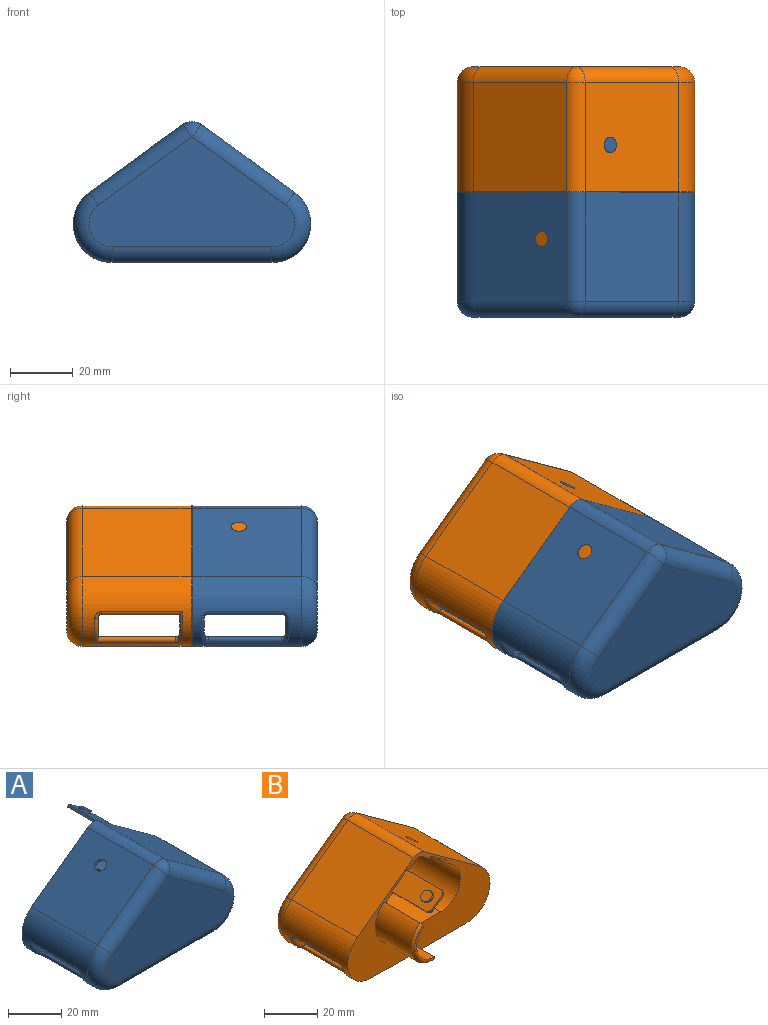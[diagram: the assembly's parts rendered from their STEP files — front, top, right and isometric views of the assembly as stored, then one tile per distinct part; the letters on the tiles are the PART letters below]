
ASSEMBLY  parts=2 mates=1
PART A: 71 faces, bbox 77.8x60x46 mm
  f0: cylinder r=1mm len=23.45mm, axis (0,-1,0), area 62.9mm2, adj f1,f13,f53,f62
  f1: bspline ~2.2x1.73mm, area 3.7mm2, adj f0,f13,f53,f55,f57
  f2: cylinder r=1mm len=23.45mm, axis (0,-1,0), area 62.9mm2, adj f3,f6,f12,f53
  f3: bspline ~2.2x1.73mm, area 3.7mm2, adj f2,f5,f12,f53,f57
  f4: bspline ~3.05x2.82mm, area 4mm2, adj f13,f58,f62,f65
  f5: bspline ~3.05x2.82mm, area 4mm2, adj f3,f12,f57,f61
  f6: bspline ~2.2x1.73mm, area 3.7mm2, adj f2,f12,f53,f65,f68
  f7: plane 75.76x45mm, normal (0,1,0), area 1366.3mm2, adj f8,f9,f10,f12,f13,f14,f15,f16
  f8: plane 51.04x35mm, normal (0,0,-1), area 1786.4mm2, adj f7,f12,f13,f25
  f9: plane 35x29.85mm, normal (0.59,0,0.81), area 1291.2mm2, adj f7,f12,f14,f26
  f10: plane 35x29.85mm, normal (-0.59,0,0.81), area 1271.6mm2, adj f7,f13,f14,f22,f32
  f11: plane 65.76x35mm, normal (0,-1,0), area 1488.7mm2, adj f22,f23,f25,f26,f27
  f12: cylinder r=12.36mm len=35mm, axis (0,-1,0), area 748.5mm2, adj f2,f3,f5,f6,f7,f8,f9,f27
  f13: cylinder r=12.36mm len=35mm, axis (0,-1,0), area 748.5mm2, adj f0,f1,f4,f7,f8,f10,f23,f54
  f14: cylinder r=5mm len=35mm, axis (0,1,0), area 219.9mm2, adj f7,f9,f10,f24
  f15: plane 38x20.51mm, normal (0,0,1), area 779.4mm2, adj f7,f18,f20,f46
  f16: plane 58x13.66mm, normal (-0.59,0,-0.81), area 841.2mm2, adj f7,f18,f21,f35,f36,f38,f48,f49
  f17: plane 38x16.08mm, normal (0.59,0,-0.81), area 552.1mm2, adj f7,f18,f20,f21,f28,f29,f31,f33
  f18: plane 44.23x31mm, normal (0,1,0), area 991.7mm2, adj f15,f16,f17,f19,f20,f21,f46,f48
  f19: cylinder r=10.36mm len=19.66mm, axis (0,-1,0), area 444mm2, adj f18,f46,f47,f48
  f20: cylinder r=10.36mm len=38mm, axis (0,-1,0), area 989.5mm2, adj f7,f15,f17,f18
  f21: cylinder r=3mm len=38mm, axis (0,1,0), area 143.3mm2, adj f7,f16,f17,f18
  f22: cylinder r=5mm len=32.79mm, axis (0.81,0,0.59), area 289.7mm2, adj f10,f11,f23,f24
  f23: torus R=7.36mm, axis (0,-1,0), area 208.1mm2, adj f11,f13,f22,f25
  f24: sphere r=5mm, area 48.5mm2, adj f14,f22,f26
  f25: cylinder r=5mm len=51.04mm, axis (-1,0,0), area 400.9mm2, adj f8,f11,f23,f27
  f26: cylinder r=5mm len=32.79mm, axis (0.81,0,-0.59), area 289.7mm2, adj f9,f11,f24,f27
  f27: torus R=7.36mm, axis (0,-1,0), area 208.1mm2, adj f11,f12,f25,f26
  f28: plane 18.5x0.81mm, normal (0.81,0,0.59), area 18.5mm2, adj f7,f17,f30,f33
  f29: plane 18.5x0.81mm, normal (-0.81,0,-0.59), area 18.5mm2, adj f7,f17,f30,f34
  f30: plane 20.5x8.09mm, normal (0.59,0,-0.81), area 183.6mm2, adj f7,f28,f29,f31,f32,f33,f34
  f31: plane 5.44x4.34mm, normal (0,1,0), area 6mm2, adj f17,f30,f33,f34
  f32: cylinder r=2.5mm len=5mm, axis (-0.59,0,0.81), area 15.7mm2, adj f10,f30
  f33: cylinder r=2mm len=2.21mm, axis (0.59,0,-0.81), area 3.1mm2, adj f17,f28,f30,f31
  f34: cylinder r=2mm len=2.21mm, axis (-0.59,0,0.81), area 3.1mm2, adj f17,f29,f30,f31
  f35: plane 19x0.81mm, normal (-0.81,0,0.59), area 19mm2, adj f7,f16,f37,f49
  f36: plane 20x0.81mm, normal (0.81,0,-0.59), area 20mm2, adj f7,f16,f37,f38
  f37: plane 20x8.09mm, normal (0.59,0,0.81), area 181.7mm2, adj f7,f35,f36,f38,f39,f49
  f38: plane 7.87x6.1mm, normal (0,1,0), area 9mm2, adj f16,f36,f37,f49
  f39: cylinder r=2.4mm len=4.8mm, axis (-0.59,0,-0.81), area 15.1mm2, adj f37,f40
  f40: plane 4.8x3.88mm, normal (0.59,0,0.81), area 18.1mm2, adj f39
  f41: cylinder r=10.36mm len=19mm, axis (0,-1,0), area 494.7mm2, adj f7,f42,f43,f45
  f42: plane 20x0.81mm, normal (-0.81,0,0.59), area 19.5mm2, adj f7,f41,f44,f45
  f43: plane 20x1mm, normal (-1,0,0), area 19.5mm2, adj f7,f41,f44,f45
  f44: cylinder r=9.36mm len=40mm, axis (0,-1,0), area 941mm2, adj f42,f43,f45,f46,f47,f48
  f45: cone r=9.36mm half-angle=45deg, axis (0,-1,0), area 35mm2, adj f41,f42,f43,f44
  f46: cylinder r=5mm len=38mm, axis (0,-1,0), area 89.6mm2, adj f7,f15,f18,f19,f44,f47
  f47: torus R=5.36mm, axis (0,1,0), area 86.7mm2, adj f19,f44,f46,f48
  f48: cylinder r=5mm len=38mm, axis (0,-1,0), area 89.6mm2, adj f7,f16,f18,f19,f44,f47
  f49: cylinder r=1mm len=1.4mm, axis (0.59,0,0.81), area 1.6mm2, adj f16,f35,f37,f38
  f50: plane 72.85x5mm, normal (0,-1,0), area 352.1mm2, adj f58,f65,f66,f70
  f51: plane 73.64x24mm, normal (0,0,-1), area 1767.3mm2, adj f59,f60,f66,f67
  f52: plane 72.85x5mm, normal (0,1,0), area 352.1mm2, adj f54,f57,f60,f61
  f53: plane 61.12x24mm, normal (0,0,1), area 1467mm2, adj f0,f1,f2,f3,f6,f57,f62,f65
  f54: torus R=11.36mm, axis (0,1,0), area 9.8mm2, adj f13,f52,f55,f56
  f55: bspline ~3.14x2.61mm, area 4mm2, adj f1,f13,f54,f57
  f56: bspline ~2.49x2.45mm, area 3.4mm2, adj f13,f54,f59,f60
  f57: cylinder r=1mm len=66.81mm, axis (-1,0,0), area 99.9mm2, adj f1,f3,f5,f52,f53,f55
  f58: torus R=11.36mm, axis (0,1,0), area 9.8mm2, adj f4,f13,f50,f63
  f59: cylinder r=1mm len=24mm, axis (0,-1,0), area 35.2mm2, adj f13,f51,f56,f63
  f60: cylinder r=1mm len=73.64mm, axis (1,0,0), area 115.1mm2, adj f51,f52,f56,f64
  f61: torus R=11.36mm, axis (0,1,0), area 9.8mm2, adj f5,f12,f52,f64
  f62: bspline ~2.2x1.73mm, area 3.7mm2, adj f0,f4,f13,f53,f65
  f63: bspline ~2.68x2.34mm, area 3.4mm2, adj f13,f58,f59,f66
  f64: bspline ~2.68x2.34mm, area 3.4mm2, adj f12,f60,f61,f67
  f65: cylinder r=1mm len=66.81mm, axis (1,0,0), area 99.9mm2, adj f4,f6,f50,f53,f62,f68
  f66: cylinder r=1mm len=73.64mm, axis (-1,0,0), area 115.1mm2, adj f50,f51,f63,f69
  f67: cylinder r=1mm len=24mm, axis (0,-1,0), area 35.2mm2, adj f12,f51,f64,f69
  f68: bspline ~3.14x2.61mm, area 4mm2, adj f6,f12,f65,f70
  f69: bspline ~2.49x2.45mm, area 3.4mm2, adj f12,f66,f67,f70
  f70: torus R=11.36mm, axis (0,1,0), area 9.8mm2, adj f12,f50,f68,f69
PART B: 63 faces, bbox 77.8x60x46 mm
  f0: bspline ~2.2x1.73mm, area 3.7mm2, adj f2,f9,f46,f53,f58
  f1: bspline ~2.2x1.73mm, area 3.7mm2, adj f6,f46,f58,f61,f62
  f2: bspline ~3.05x2.82mm, area 4mm2, adj f0,f9,f54,f58
  f3: plane 75.76x45mm, normal (0,-1,0), area 1337.1mm2, adj f6,f7,f8,f9,f10,f11,f13,f14
  f4: cylinder r=10.36mm len=18.74mm, axis (0,-1,0), area 442.7mm2, adj f12,f14,f17,f42
  f5: plane 65.76x35mm, normal (0,1,0), area 1488.7mm2, adj f19,f20,f21,f22,f23
  f6: cylinder r=12.36mm len=35mm, axis (0,-1,0), area 743.7mm2, adj f1,f3,f8,f11,f21,f56,f57,f59
  f7: cylinder r=5mm len=35mm, axis (0,1,0), area 219.9mm2, adj f3,f8,f10,f18
  f8: plane 35x29.85mm, normal (-0.59,0,0.81), area 1291.2mm2, adj f3,f6,f7,f19
  f9: cylinder r=12.36mm len=35mm, axis (0,-1,0), area 743.7mm2, adj f0,f2,f3,f10,f11,f22,f50,f51
  f10: plane 35x29.85mm, normal (0.59,0,0.81), area 1271.6mm2, adj f3,f7,f9,f20,f36
  f11: plane 51.04x35mm, normal (0,0,-1), area 1786.4mm2, adj f3,f6,f9,f23
  f12: plane 44.23x31mm, normal (0,-1,0), area 992mm2, adj f4,f13,f14,f15,f16,f17
  f13: cylinder r=3mm len=38mm, axis (0,1,0), area 143.3mm2, adj f3,f12,f14,f16
  f14: plane 58x16.08mm, normal (0.59,0,-0.81), area 953.7mm2, adj f3,f4,f12,f13,f24,f25,f26,f30
  f15: cylinder r=10.36mm len=38mm, axis (0,-1,0), area 989.5mm2, adj f3,f12,f16,f17
  f16: plane 38x16.08mm, normal (-0.59,0,-0.81), area 555.8mm2, adj f3,f12,f13,f15,f32,f33,f34,f44
  f17: plane 38x23.51mm, normal (0,0,1), area 893.4mm2, adj f3,f4,f12,f15,f40
  f18: sphere r=5mm, area 40mm2, adj f7,f19,f20
  f19: cylinder r=5mm len=32.79mm, axis (-0.81,0,-0.59), area 289.7mm2, adj f5,f8,f18,f21
  f20: cylinder r=5mm len=32.79mm, axis (-0.81,0,0.59), area 289.7mm2, adj f5,f10,f18,f22
  f21: torus R=7.36mm, axis (0,-1,0), area 208.1mm2, adj f5,f6,f19,f23
  f22: torus R=7.36mm, axis (0,-1,0), area 208.1mm2, adj f5,f9,f20,f23
  f23: cylinder r=5mm len=51.04mm, axis (1,0,0), area 400.9mm2, adj f5,f11,f21,f22
  f24: plane 5.44x4.34mm, normal (0,-1,0), area 6mm2, adj f14,f27,f30,f31
  f25: plane 18x0.81mm, normal (0.81,0,0.59), area 18mm2, adj f3,f14,f27,f30
  f26: plane 18x0.81mm, normal (-0.81,0,-0.59), area 18mm2, adj f3,f14,f27,f31
  f27: plane 20x8.09mm, normal (-0.59,0,0.81), area 180.2mm2, adj f3,f24,f25,f26,f28,f30,f31
  f28: cylinder r=2.4mm len=4.8mm, axis (0.59,0,-0.81), area 15.1mm2, adj f27,f29
  f29: plane 4.8x3.88mm, normal (-0.59,0,0.81), area 18.1mm2, adj f28
  f30: cylinder r=2mm len=2.21mm, axis (-0.59,0,0.81), area 3.1mm2, adj f14,f24,f25,f27
  f31: cylinder r=2mm len=2.21mm, axis (0.59,0,-0.81), area 3.1mm2, adj f14,f24,f26,f27
  f32: plane 7.06x5.51mm, normal (0,-1,0), area 8mm2, adj f16,f35,f44,f45
  f33: plane 19x0.81mm, normal (0.81,0,-0.59), area 19mm2, adj f3,f16,f35,f44
  f34: plane 19x0.81mm, normal (-0.81,0,0.59), area 19mm2, adj f3,f16,f35,f45
  f35: plane 20x8.09mm, normal (-0.59,0,-0.81), area 179.9mm2, adj f3,f32,f33,f34,f36,f44,f45
  f36: cylinder r=2.5mm len=5mm, axis (0.59,0,0.81), area 15.7mm2, adj f10,f35
  f37: cylinder r=9.36mm len=40mm, axis (0,1,0), area 941mm2, adj f38,f40,f41,f42
  f38: plane 41x1.62mm, normal (0.81,0,0.59), area 60mm2, adj f3,f14,f37,f39,f41,f42,f43
  f39: cylinder r=11.36mm len=20.55mm, axis (0,1,0), area 542.5mm2, adj f3,f38,f40,f43
  f40: plane 41x2mm, normal (1,0,0), area 60mm2, adj f3,f17,f37,f39,f41,f42,f43
  f41: plane 18.74x10.36mm, normal (0,-1,0), area 24.8mm2, adj f37,f38,f40,f43
  f42: cone r=9.36mm half-angle=45deg, axis (0,1,0), area 35mm2, adj f4,f37,f38,f40
  f43: cone r=11.36mm half-angle=45deg, axis (0,1,0), area 38.6mm2, adj f38,f39,f40,f41
  f44: cylinder r=1mm len=1.4mm, axis (-0.59,0,-0.81), area 1.6mm2, adj f16,f32,f33,f35
  f45: cylinder r=1mm len=1.4mm, axis (0.59,0,0.81), area 1.6mm2, adj f16,f32,f34,f35
  f46: plane 61.12x25mm, normal (0,0,1), area 1528.1mm2, adj f0,f1,f47,f53,f58,f62
  f47: plane 72.85x6.52mm, normal (0,-1,0), area 418.5mm2, adj f46,f50,f53,f55,f60,f62
  f48: plane 73.64x25.01mm, normal (0,0,-1), area 1840.9mm2, adj f49,f51,f54,f55,f56,f59
  f49: plane 73.34x6mm, normal (0,1,0), area 425.2mm2, adj f48,f54,f58,f59
  f50: torus R=11.36mm, axis (0,-1,0), area 14.8mm2, adj f9,f47,f52,f53
  f51: cylinder r=1mm len=26mm, axis (0,-1,0), area 37.4mm2, adj f9,f48,f52,f54
  f52: bspline ~2.49x2.45mm, area 3.4mm2, adj f9,f50,f51,f55
  f53: cylinder r=1mm len=25.73mm, axis (0,-1,0), area 67.1mm2, adj f0,f9,f46,f47,f50
  f54: torus R=11.36mm, axis (0,-1,0), area 12.2mm2, adj f2,f9,f48,f49,f51
  f55: cylinder r=1mm len=73.64mm, axis (1,0,0), area 115.1mm2, adj f47,f48,f52,f57
  f56: cylinder r=1mm len=26mm, axis (0,-1,0), area 37.4mm2, adj f6,f48,f57,f59
  f57: bspline ~2.68x2.34mm, area 3.4mm2, adj f6,f55,f56,f60
  f58: cylinder r=1mm len=66.81mm, axis (1,0,0), area 99.9mm2, adj f0,f1,f2,f46,f49,f61
  f59: torus R=11.36mm, axis (0,-1,0), area 12.2mm2, adj f6,f48,f49,f56,f61
  f60: torus R=11.36mm, axis (0,-1,0), area 14.8mm2, adj f6,f47,f57,f62
  f61: bspline ~3.14x2.61mm, area 4mm2, adj f1,f6,f58,f59
  f62: cylinder r=1mm len=25.73mm, axis (0,-1,0), area 67.1mm2, adj f1,f6,f46,f47,f60
PLACE A t=(-7.87,42.74,-20.64)mm
PLACE B t=(-7.87,-37.31,-20.64)mm
MATE slider A.f11 <-> B.f5  axis (0,-1,0) through (-7.87,2.74,-29.09)mm
